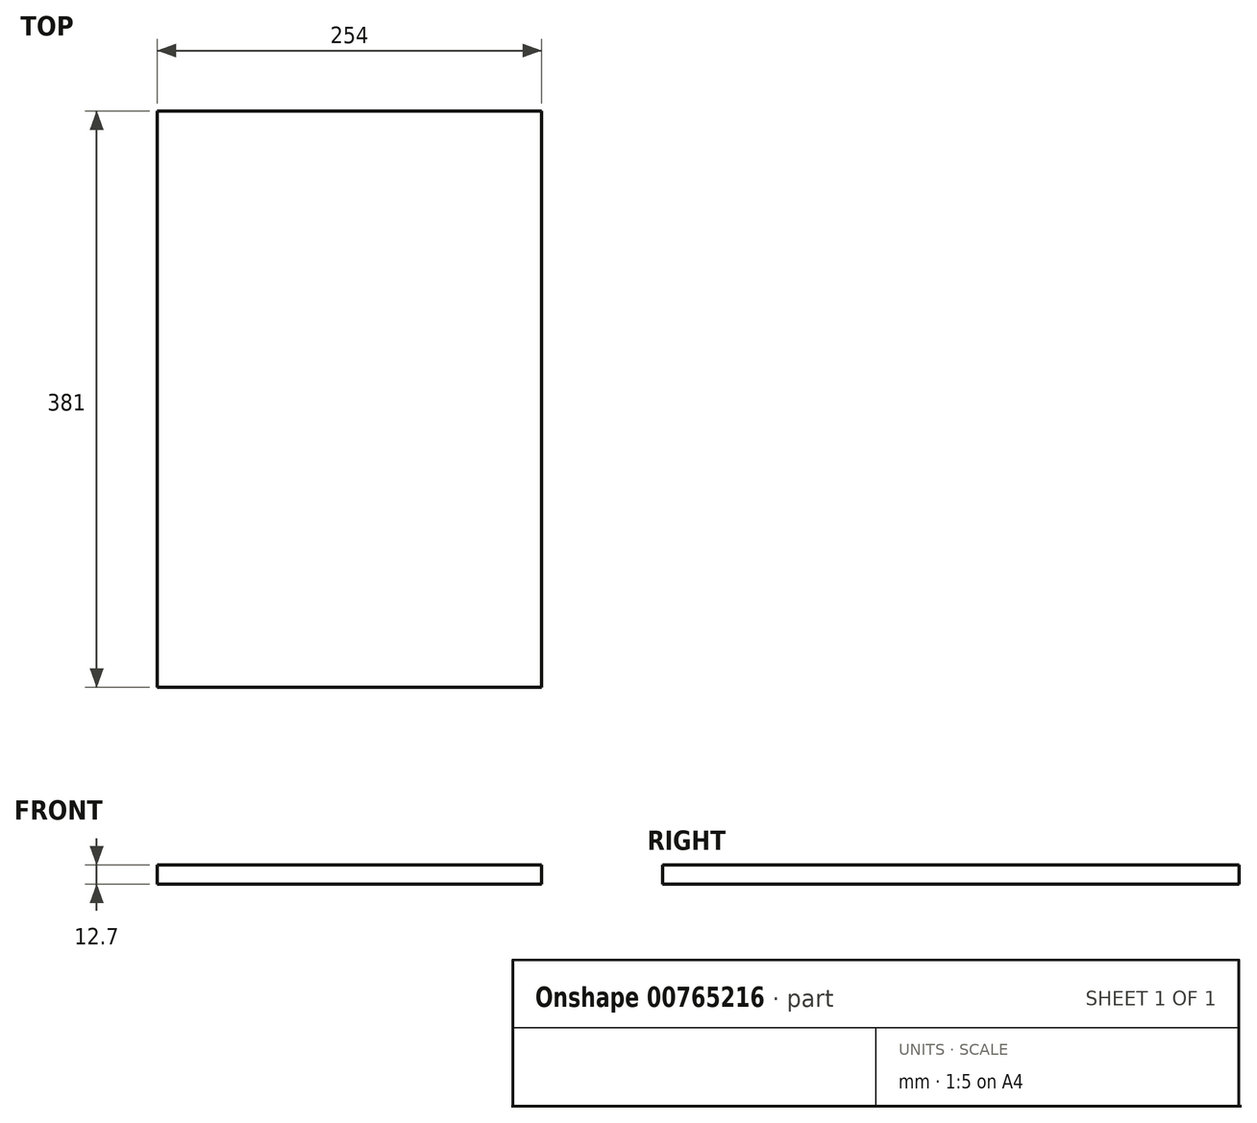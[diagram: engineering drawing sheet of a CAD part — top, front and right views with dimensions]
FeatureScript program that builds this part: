
annotation { "Feature Type Name" : "Feature", "Feature Type Description" : "" }
export const myFeature = defineFeature(function(context is Context, id is Id, definition is map)
    precondition{}
    {
        {
            var Q0;
            Q0=qCreatedBy(makeId("Front.planeOp"),FACE);
            var sketch = newSketch(context, id + "F0", { "sketchPlane" : qUnion([Q0])});
            skLineSegment(sketch, "E0.bottom", {"start": v(-127, 6.35) * mm, "end": v(127, 6.35) * mm});
            skLineSegment(sketch, "E0.top", {"start": v(-127, -6.35) * mm, "end": v(127, -6.35) * mm});
            skLineSegment(sketch, "E0.left", {"start": v(-127, 6.35) * mm, "end": v(-127, -6.35) * mm});
            skLineSegment(sketch, "E0.right", {"start": v(127, 6.35) * mm, "end": v(127, -6.35) * mm});
            skPoint(sketch, "E0.middle", {"position": v(0, 0) * mm});
            skSolve(sketch);
        }
        {
            var Q0;
            Q0=makeQuery(id+"F0.imprint","IMPRINT",FACE,{"disambiguationData":[TD([[makeQuery(id+"F0.imprint","IMPRINT",EDGE,{"derivedFrom":sQuery(id+"F0.wireOp",EDGE,"E0.bottom")}),-1.0]])]});
            extrude(context, id + "F1", {"entities" : qUnion([Q0]), "depth" : 381 * mm, "offsetDistance" : 25.4 * mm});
        }
    });
